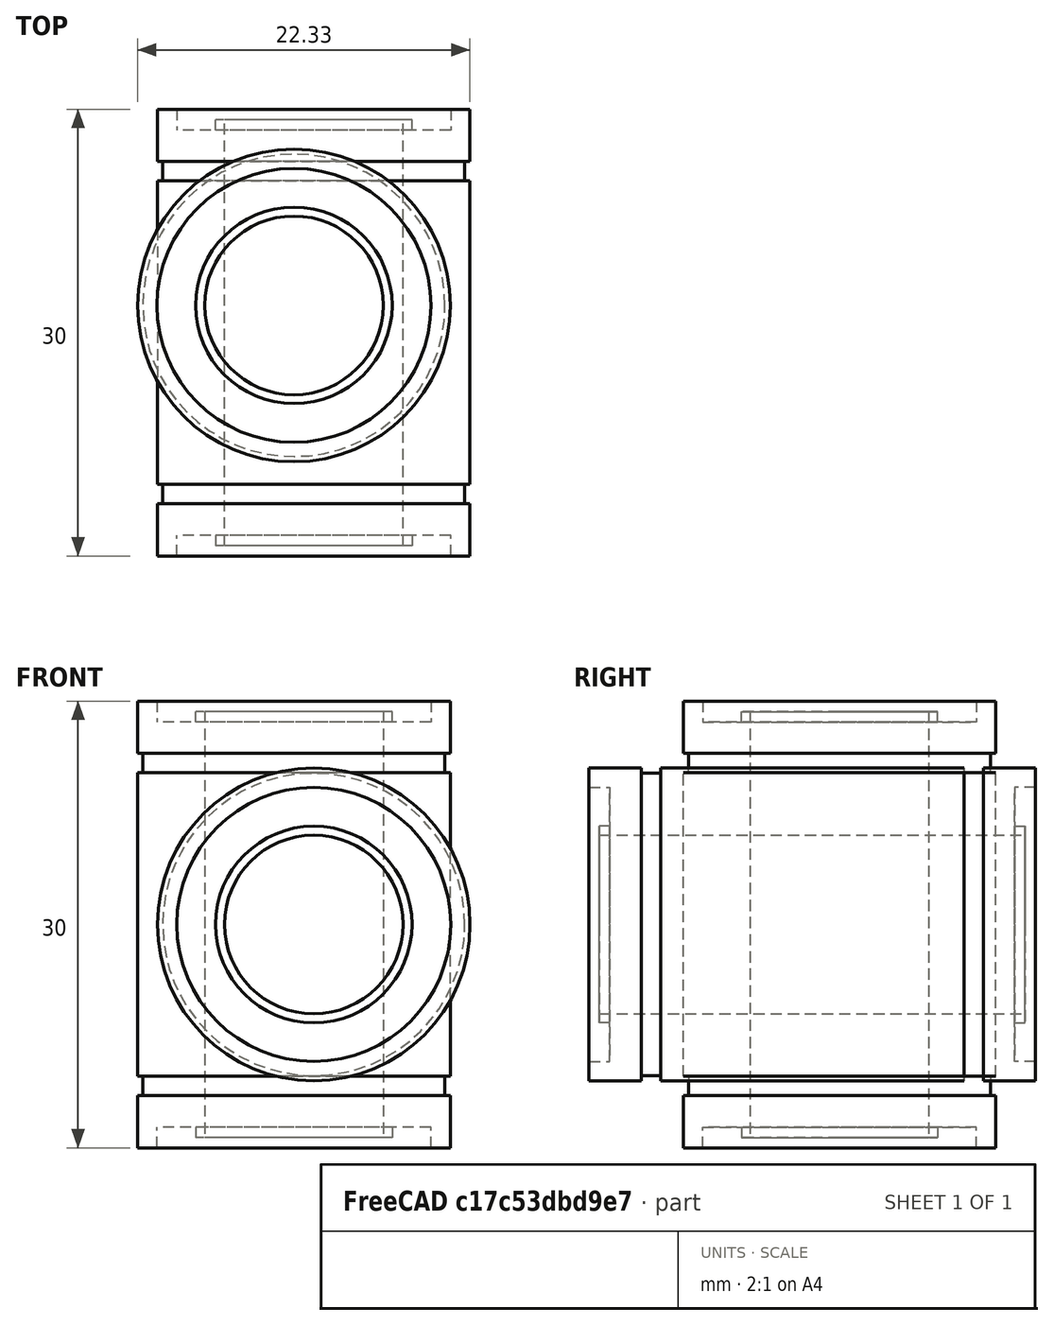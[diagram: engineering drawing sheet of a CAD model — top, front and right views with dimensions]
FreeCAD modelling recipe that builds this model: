
FCSTD DOCUMENT  (FreeCAD 0.15R4630 (Git))
Label: LM12uu
Comment: Modified LM8UU to LM12UU specs by furanshishouco
License: CC-BY 3.0
LicenseURL: http://creativecommons.org/licenses/by/3.0/
objects: Sketcher::SketchObject×1, PartDesign::Revolution×1, Part::Feature×1
note: 4 computed .brp shape members not serialized (recipe doc carries the construction recipe); baked Part::Feature solids carry a one-line shape summary decoded from their .brp

FEATURE [Sketcher::SketchObject] Sketch  label="lm12uu-cross-section"
  Placement = pos=(0,0,0) rot=(1,0,0;1.5708rad)
  sketch-geometry (20):
    g0: LineSegment StartX=10.5 StartY=-15 StartZ=0 EndX=10.5 EndY=-11.5 EndZ=0
    g1: LineSegment StartX=10.5 StartY=10.2 StartZ=0 EndX=10.15 EndY=10.2 EndZ=0
    g2: LineSegment StartX=10.15 StartY=10.2 StartZ=0 EndX=10.15 EndY=11.5 EndZ=0
    g3: LineSegment StartX=10.15 StartY=11.5 StartZ=0 EndX=10.5 EndY=11.5 EndZ=0
    g4: LineSegment StartX=10.5 StartY=11.5 StartZ=0 EndX=10.5 EndY=15 EndZ=0
    g5: LineSegment StartX=10.5 StartY=15 StartZ=0 EndX=9.2 EndY=15 EndZ=0
    g6: LineSegment StartX=9.2 StartY=15 StartZ=0 EndX=9.2 EndY=13.6 EndZ=0
    g7: LineSegment StartX=9.2 StartY=13.6 StartZ=0 EndX=6.6 EndY=13.6 EndZ=0
    g8: LineSegment StartX=6.6 StartY=13.6 StartZ=0 EndX=6.6 EndY=14.3 EndZ=0
    g9: LineSegment StartX=6.6 StartY=14.3 StartZ=0 EndX=6 EndY=14.3 EndZ=0
    g10: LineSegment StartX=6 StartY=14.3 StartZ=0 EndX=6 EndY=-14.3 EndZ=0
    g11: LineSegment StartX=10.5 StartY=-10.2 StartZ=0 EndX=10.15 EndY=-10.2 EndZ=0
    g12: LineSegment StartX=10.15 StartY=-11.5 StartZ=0 EndX=10.5 EndY=-11.5 EndZ=0
    g13: LineSegment StartX=10.5 StartY=-10.2 StartZ=0 EndX=10.5 EndY=10.2 EndZ=0
    g14: LineSegment StartX=10.15 StartY=-10.2 StartZ=0 EndX=10.15 EndY=-11.5 EndZ=0
    g15: LineSegment StartX=10.5 StartY=-15 StartZ=0 EndX=9.2 EndY=-15 EndZ=0
    g16: LineSegment StartX=9.2 StartY=-15 StartZ=0 EndX=9.2 EndY=-13.6 EndZ=0
    g17: LineSegment StartX=9.2 StartY=-13.6 StartZ=0 EndX=6.6 EndY=-13.6 EndZ=0
    g18: LineSegment StartX=6.6 StartY=-13.6 StartZ=0 EndX=6.6 EndY=-14.3 EndZ=0
    g19: LineSegment StartX=6.6 StartY=-14.3 StartZ=0 EndX=6 EndY=-14.3 EndZ=0
  constraints (58):
    c: Coincident(g13,g1)
    c: Coincident(g1,g2)
    c: Vertical(g2)
    c: Coincident(g2,g3)
    c: Coincident(g3,g4)
    c: Vertical(g4)
    c: Coincident(g4,g5)
    c: Coincident(g5,g6)
    c: Vertical(g6)
    c: Coincident(g6,g7)
    c: Horizontal(g7)
    c: Coincident(g7,g8)
    c: Vertical(g8)
    c: Coincident(g8,g9)
    c: Horizontal(g9)
    c: Coincident(g9,g10)
    c: Vertical(g10)
    c: Horizontal(g1)
    c: Horizontal(g5)
    c: Horizontal(g3)
    c: PointOnObject(g3,g0)
    c: Symmetric(g0,g4,g-1)
    c: DistanceY(g4,g0) = -30
    c: DistanceY(g2) = 1.3
    c: DistanceX(g3) = 0.35
    c: DistanceX(g-1,g4) = 10.5
    c: DistanceX(g-1,g9) = 6
    c: DistanceX(g5) = -1.3
    c: DistanceX(g9) = -0.6
    c: DistanceY(g6) = -1.4
    c: DistanceY(g8) = 0.7
    c: Horizontal(g11)
    c: Horizontal(g12)
    c: Coincident(g13,g11)
    c: Tangent(g0,g13)
    c: Coincident(g12,g0)
    c: PointOnObject(g14,g11)
    c: Coincident(g14,g12)
    c: Vertical(g14)
    c: Symmetric(g1,g11,g-1)
    c: DistanceY(g13) = 20.4
    c: Equal(g14,g2)
    c: Coincident(g0,g15)
    c: Horizontal(g15)
    c: Coincident(g15,g16)
    c: Vertical(g16)
    c: Coincident(g16,g17)
    c: Horizontal(g17)
    c: Coincident(g17,g18)
    c: Vertical(g18)
    c: Coincident(g18,g19)
    c: Horizontal(g19)
    c: Coincident(g10,g19)
    c: Symmetric(g10,g9,g-1)
    c: Symmetric(g16,g6,g-1)
    c: Symmetric(g17,g7,g-1)
    c: Coincident(g14,g11)
    c: PointOnObject(g11,g2)
FEATURE [PartDesign::Revolution] Revolution  label="LM12uu"
  Angle = 360
  Axis = (0,0,1)
  Base = (0,0,0)
  Placement = pos=(0,0,0) rot=(1,0,0;1.5708rad)
  ReferenceAxis = -> Sketch [V_Axis]
  Reversed = true
  Sketch = -> Sketch
FEATURE [Part::Feature] Revolution001  label="LM12uu001"
  Placement = pos=(1.33183,-1.82934,0.000839476) rot=(1,0,0;1.5708rad)
  shape: bbox 21 x 30 x 21 mm, 20 faces (baked)
